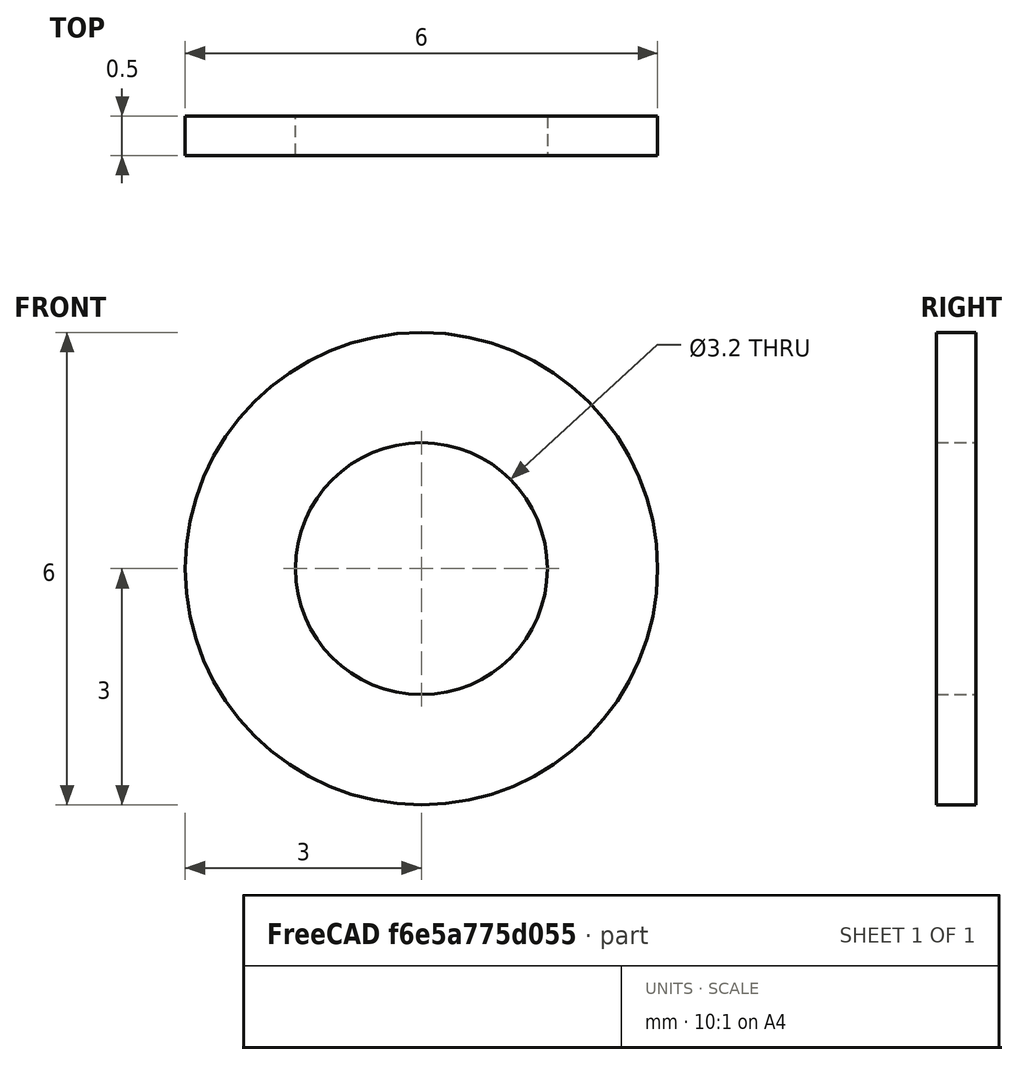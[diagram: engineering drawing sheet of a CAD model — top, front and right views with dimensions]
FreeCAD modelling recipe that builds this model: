
FCSTD DOCUMENT  (FreeCAD 0.19R)
Label: washer_M5
License: All rights reserved
LicenseURL: http://en.wikipedia.org/wiki/All_rights_reserved
objects: PartDesign::CoordinateSystem×2, Sketcher::SketchObject×1, PartDesign::Pad×1, PartDesign::Body×1
note: 6 computed .brp shape members not serialized (recipe doc carries the construction recipe); baked Part::Feature solids carry a one-line shape summary decoded from their .brp

FEATURE [Sketcher::SketchObject] Sketch
  FullyConstrained = true
  MapMode = 5
  Placement = pos=(0,0,0) rot=(1,0,0;1.5708rad)
  Support = -> [XZ_Plane]
  sketch-geometry (2):
    g0: Circle CenterX=0 CenterY=0 CenterZ=0 NormalX=0 NormalY=0 NormalZ=1 AngleXU=0 Radius=3
    g1: Circle CenterX=0 CenterY=0 CenterZ=0 NormalX=0 NormalY=0 NormalZ=1 AngleXU=0 Radius=1.6
  constraints (4):
    c: Coincident(g0,g-1)
    c: Coincident(g1,g0)
    c: Diameter(g1) = 3.2
    c: Diameter(g0) = 6
FEATURE [PartDesign::Pad] Pad
  Direction = (1,1,1)
  Length = 0.5
  Length2 = 100
  Midplane = true
  Placement = pos=(0,0,0) rot=(1,0,0;1.5708rad)
  Profile = -> Sketch
  Refine = true
  Type = 0
FEATURE [PartDesign::CoordinateSystem] Local_CS  label="Local_washer_side1"
  AttacherType = Attacher::AttachEngine3D
  MapMode = 11
  Placement = pos=(0,-0.25,0) rot=(0.57735,-0.57735,0.57735;2.0944rad)
  Support = -> [Pad]
FEATURE [PartDesign::CoordinateSystem] Local_CS001  label="Local_washer_side2"
  AttacherType = Attacher::AttachEngine3D
  MapMode = 11
  Placement = pos=(0,0.25,0) rot=(0.57735,-0.57735,0.57735;2.0944rad)
  Support = -> [Pad]
FEATURE [PartDesign::Body] Body
  Group = -> [Sketch,Pad,Local_CS,Local_CS001]
  Origin = -> Origin
  Tip = -> Pad
